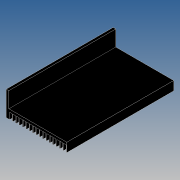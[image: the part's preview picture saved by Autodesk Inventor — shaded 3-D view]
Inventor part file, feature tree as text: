
AUTODESK INVENTOR PART (.ipt)
format: ipt  version: 2018.2 (Build 222227000, 227)  size: 175,616 bytes
history: native  units: mm
features: extrude x3, sketch x3, projected_geometry x1
ambient origin geometry x8: Origin, YZ Plane, XZ Plane, XY Plane, X Axis, Y Axis, Z Axis, Center Point
bodies: Volumenkörper1 (feature_tree)
feature tree (7):
  extrude  "Grundkörper"  Depth=81.0mm
  extrude  "Ausschnitt"  Depth=12.0mm
  extrude  "Kühlrippen"  Depth=33.0mm TaperAngle=0.0deg
  sketch  "Skizze1"  dims[d0=143.0mm d1=81.0mm]
  sketch  "Skizze2"  dims[d2=33.0mm d3=0.0mm d4=12.0mm]
  projected_geometry  "Projizierte Kontur1"
  sketch  "Skizze3"  dims[d5=3.5mm d9=33.0mm d10=0.0mm d11=1.0mm d12=8.5mm d13=3.5mm d14=170.0mm d16=4.5mm d17=10.0mm d19=10.0mm d21=33.0mm d22=0.0mm]
